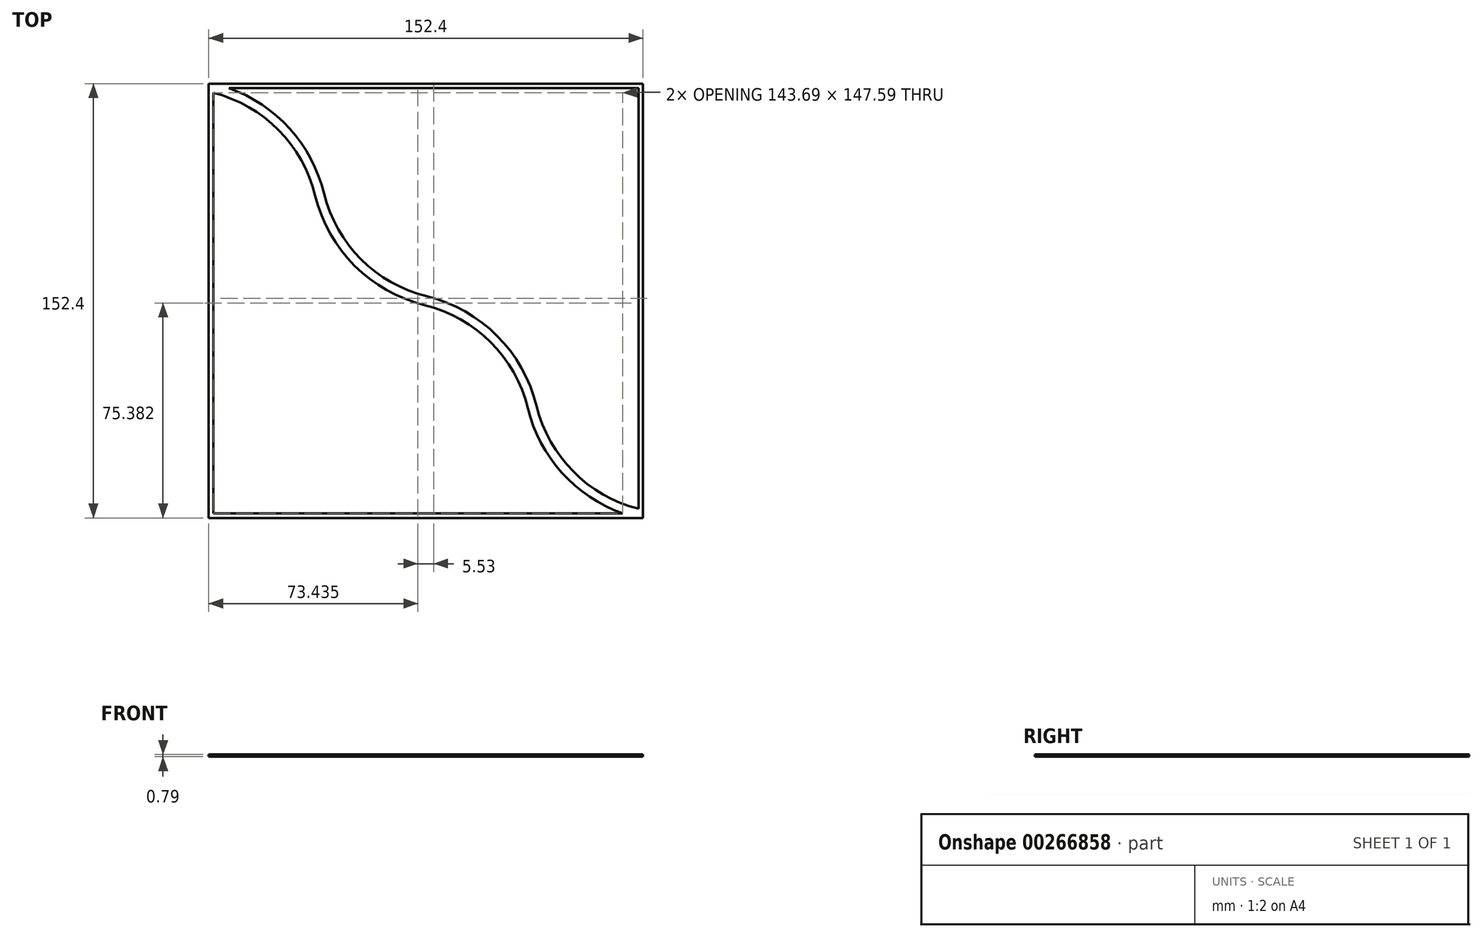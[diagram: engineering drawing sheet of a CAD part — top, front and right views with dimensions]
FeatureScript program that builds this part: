
annotation { "Feature Type Name" : "Feature", "Feature Type Description" : "" }
export const myFeature = defineFeature(function(context is Context, id is Id, definition is map)
    precondition{}
    {
        {
            var Q0;
            Q0=qCreatedBy(makeId("Top.planeOp"),FACE);
            var sketch = newSketch(context, id + "F0", { "sketchPlane" : qUnion([Q0])});
            skLineSegment(sketch, "E0.bottom", {"start": v(-76.2, 76.2) * mm, "end": v(76.2, 76.2) * mm});
            skLineSegment(sketch, "E0.top", {"start": v(-76.2, -76.2) * mm, "end": v(76.2, -76.2) * mm});
            skLineSegment(sketch, "E0.left", {"start": v(-76.2, 76.2) * mm, "end": v(-76.2, -76.2) * mm});
            skLineSegment(sketch, "E0.right", {"start": v(76.2, 76.2) * mm, "end": v(76.2, -76.2) * mm});
            skLineSegment(sketch, "E1.0", {"start": v(-74.61, 72.98) * mm, "end": v(-74.61, -74.61) * mm});
            skLineSegment(sketch, "E1.1", {"start": v(-69.08, 74.61) * mm, "end": v(74.61, 74.61) * mm});
            skLineSegment(sketch, "E1.2", {"start": v(74.61, 74.61) * mm, "end": v(74.61, -72.98) * mm});
            skLineSegment(sketch, "E1.3", {"start": v(-74.61, -74.61) * mm, "end": v(69.08, -74.61) * mm});
            skLineSegment(sketch, "E2", {"start": v(-74.61, 74.61) * mm, "end": v(74.61, -74.61) * mm, "construction": true});
            skArc(sketch, "E3", {"start": v(-37.3, 37.3) * mm, "mid": v(-50.74, 61.18) * mm, "end": v(-74.61, 74.61) * mm, "construction": true});
            skArc(sketch, "E4", {"start": v(-37.3, 37.3) * mm, "mid": v(-23.88, 13.43) * mm, "end": v(0, 0) * mm, "construction": true});
            skArc(sketch, "E5", {"start": v(37.3, -37.3) * mm, "mid": v(23.88, -13.43) * mm, "end": v(0, 0) * mm, "construction": true});
            skArc(sketch, "E6", {"start": v(37.3, -37.3) * mm, "mid": v(50.74, -61.18) * mm, "end": v(74.61, -74.61) * mm, "construction": true});
            skArc(sketch, "E7.0", {"start": v(-35.76, 37.68) * mm, "mid": v(-47.76, 60.35) * mm, "end": v(-69.08, 74.61) * mm});
            skArc(sketch, "E7.1", {"start": v(-35.76, 37.68) * mm, "mid": v(-22.75, 14.55) * mm, "end": v(0.38, 1.54) * mm});
            skArc(sketch, "E7.2", {"start": v(38.85, -36.93) * mm, "mid": v(25, -12.3) * mm, "end": v(0.38, 1.54) * mm});
            skArc(sketch, "E7.3", {"start": v(38.85, -36.93) * mm, "mid": v(51.72, -59.92) * mm, "end": v(74.61, -72.98) * mm});
            skArc(sketch, "E8.0", {"start": v(-38.85, 36.93) * mm, "mid": v(-51.72, 59.92) * mm, "end": v(-74.61, 72.98) * mm});
            skArc(sketch, "E8.1", {"start": v(-38.85, 36.93) * mm, "mid": v(-25, 12.3) * mm, "end": v(-0.38, -1.54) * mm});
            skArc(sketch, "E8.2", {"start": v(35.76, -37.68) * mm, "mid": v(22.75, -14.55) * mm, "end": v(-0.38, -1.54) * mm});
            skArc(sketch, "E8.3", {"start": v(35.76, -37.68) * mm, "mid": v(47.76, -60.35) * mm, "end": v(69.08, -74.61) * mm});
            skSolve(sketch);
        }
        {
            var Q0;
            Q0=makeQuery(id+"F0.imprint","IMPRINT",FACE,{"disambiguationData":[TD([[makeQuery(id+"F0.imprint","IMPRINT",EDGE,{"derivedFrom":sQuery(id+"F0.wireOp",EDGE,"E0.bottom")}),-1.0]])]});
            extrude(context, id + "F1", {"entities" : qUnion([Q0]), "depth" : 0.8 * mm});
        }
    });
